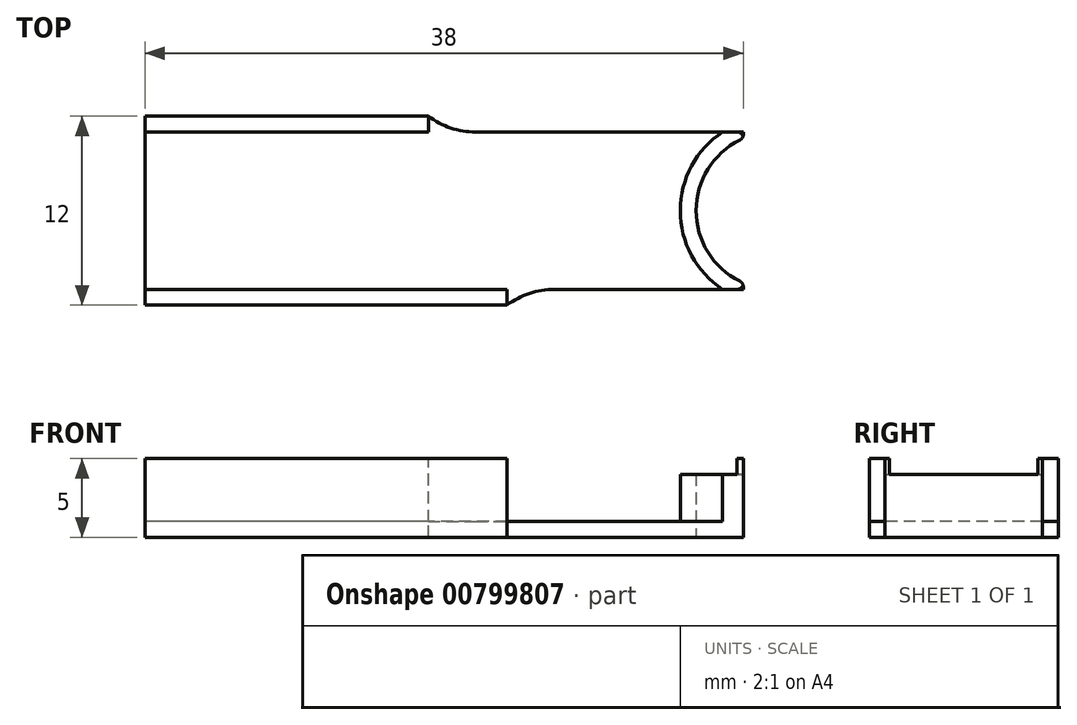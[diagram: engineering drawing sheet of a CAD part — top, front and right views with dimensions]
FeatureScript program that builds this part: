
annotation { "Feature Type Name" : "Feature", "Feature Type Description" : "" }
export const myFeature = defineFeature(function(context is Context, id is Id, definition is map)
    precondition{}
    {
        {
            var Q0;
            Q0=qCreatedBy(makeId("Top.planeOp"),FACE);
            var sketch = newSketch(context, id + "F0", { "sketchPlane" : qUnion([Q0])});
            skLineSegment(sketch, "E0.bottom", {"start": v(0, 0) * mm, "end": v(38, 0) * mm});
            skLineSegment(sketch, "E0.top", {"start": v(0, -12) * mm, "end": v(38, -12) * mm});
            skLineSegment(sketch, "E0.left", {"start": v(0, 0) * mm, "end": v(0, -12) * mm});
            skLineSegment(sketch, "E0.right", {"start": v(38, 0) * mm, "end": v(38, -1.42) * mm});
            skArc(sketch, "E1", {"start": v(38, -1.42) * mm, "mid": v(35, -6) * mm, "end": v(38, -10.58) * mm});
            skPoint(sketch, "E1.centerSnap0", {"position": v(38, -6) * mm});
            skLineSegment(sketch, "E2.trimOffspring", {"start": v(38, -10.58) * mm, "end": v(38, -12) * mm});
            skSolve(sketch);
        }
        {
            var Q0;
            Q0=makeQuery(id+"F0.imprint","IMPRINT",FACE,{"disambiguationData":[TD([[makeQuery(id+"F0.imprint","IMPRINT",EDGE,{"derivedFrom":sQuery(id+"F0.wireOp",EDGE,"E0.bottom")}),-1.0]])]});
            extrude(context, id + "F1", {"entities" : qUnion([Q0]), "depth" : 5 * mm, "offsetDistance" : 25 * mm});
        }
        {
            var Q0;
            Q0=makeQuery(id+"F1.opExtrude","CAP_FACE",FACE,{"disambiguationData":[OSD([sQuery(id+"F0.wireOp",EDGE,"E0.bottom"),sQuery(id+"F0.wireOp",EDGE,"E0.top"),sQuery(id+"F0.wireOp",EDGE,"E0.left"),sQuery(id+"F0.wireOp",EDGE,"E0.right"),sQuery(id+"F0.wireOp",EDGE,"E1"),sQuery(id+"F0.wireOp",EDGE,"E2.trimOffspring")])],"isStart":false});
            var sketch = newSketch(context, id + "F2", { "sketchPlane" : qUnion([Q0])});
            skArc(sketch, "E3.0", {"start": v(38, -1.42) * mm, "mid": v(35, -6) * mm, "end": v(38, -10.58) * mm});
            skArc(sketch, "E4", {"start": v(38, -0.34) * mm, "mid": v(34, -6) * mm, "end": v(38, -11.66) * mm});
            skLineSegment(sketch, "E5", {"start": v(38, -0.34) * mm, "end": v(38, 0) * mm});
            skLineSegment(sketch, "E6", {"start": v(18, -1) * mm, "end": v(0, -1) * mm});
            skLineSegment(sketch, "E7", {"start": v(38, -11.66) * mm, "end": v(38, -12) * mm});
            skLineSegment(sketch, "E8", {"start": v(38, -12) * mm, "end": v(23, -12) * mm});
            skLineSegment(sketch, "E9", {"start": v(23, -12) * mm, "end": v(23, -11) * mm});
            skLineSegment(sketch, "E10", {"start": v(23, -11) * mm, "end": v(0, -11) * mm});
            skLineSegment(sketch, "E11", {"start": v(0, -11) * mm, "end": v(0, -1) * mm});
            skLineSegment(sketch, "E12", {"start": v(18, -1) * mm, "end": v(18, 0) * mm});
            skLineSegment(sketch, "E13", {"start": v(18, 0) * mm, "end": v(38, 0) * mm});
            skSolve(sketch);
        }
        {
            var Q0;
            Q0=makeQuery(id+"F2.imprint","IMPRINT",FACE,{"disambiguationData":[TD([[makeQuery(id+"F2.imprint","IMPRINT",EDGE,{"derivedFrom":sQuery(id+"F2.wireOp",EDGE,"E4")}),-1.0]])]});
            extrude(context, id + "F3", {"entities" : qUnion([Q0]), "operationType" : NewBodyOperationType.REMOVE, "oppositeDirection" : true, "depth" : 4 * mm, "offsetDistance" : 25 * mm});
        }
        {
            var Q0;
            Q0=makeQuery(id+"F1.opExtrude","CAP_FACE",FACE,{"disambiguationData":[OSD([sQuery(id+"F0.wireOp",EDGE,"E0.bottom"),sQuery(id+"F0.wireOp",EDGE,"E0.top"),sQuery(id+"F0.wireOp",EDGE,"E0.left"),sQuery(id+"F0.wireOp",EDGE,"E0.right"),sQuery(id+"F0.wireOp",EDGE,"E1"),sQuery(id+"F0.wireOp",EDGE,"E2.trimOffspring")])],"isStart":true});
            var sketch = newSketch(context, id + "F4", { "sketchPlane" : qUnion([Q0])});
            skLineSegment(sketch, "E14.bottom", {"start": v(38, 12) * mm, "end": v(23, 12) * mm});
            skLineSegment(sketch, "E14.top", {"start": v(38, 11) * mm, "end": v(23, 11) * mm});
            skLineSegment(sketch, "E14.left", {"start": v(38, 12) * mm, "end": v(38, 11) * mm});
            skLineSegment(sketch, "E14.right", {"start": v(23, 12) * mm, "end": v(23, 11) * mm});
            skLineSegment(sketch, "E15.bottom", {"start": v(38, 0) * mm, "end": v(18, 0) * mm});
            skLineSegment(sketch, "E15.top", {"start": v(38, 1) * mm, "end": v(18, 1) * mm});
            skLineSegment(sketch, "E15.left", {"start": v(38, 0) * mm, "end": v(38, 1) * mm});
            skLineSegment(sketch, "E15.right", {"start": v(18, 0) * mm, "end": v(18, 1) * mm});
            skSolve(sketch);
        }
        {
            var Q0;
            Q0=makeQuery(id+"F4.imprint","IMPRINT",FACE,{"disambiguationData":[TD([[makeQuery(id+"F4.imprint","IMPRINT",EDGE,{"derivedFrom":sQuery(id+"F4.wireOp",EDGE,"E14.bottom")}),-1.0]])]});
            var Q1;
            Q1=makeQuery(id+"F4.imprint","IMPRINT",FACE,{"disambiguationData":[TD([[makeQuery(id+"F4.imprint","IMPRINT",EDGE,{"derivedFrom":sQuery(id+"F4.wireOp",EDGE,"E15.bottom")}),1.0]])]});
            extrude(context, id + "F5", {"entities" : qUnion([Q0, Q1]), "operationType" : NewBodyOperationType.REMOVE, "oppositeDirection" : true, "depth" : 25 * mm, "offsetDistance" : 25 * mm});
        }
        {
            var Q0;
            Q0=makeQuery(id+"F1.opExtrude","SWEPT_EDGE",EDGE,{"disambiguationData":[OSD([sQuery(id+"F0.wireOp",EDGE,"E1"),sQuery(id+"F0.wireOp",EDGE,"E2.trimOffspring")])]});
            var Q1;
            Q1=makeQuery(id+"F5.boolean.opBoolean","COPY",EDGE,{"derivedFrom":makeQuery(id+"F5.opExtrude","SWEPT_EDGE",EDGE,{"disambiguationData":[OSD([sQuery(id+"F0.wireOp",EDGE,"E2.trimOffspring"),sQuery(id+"F4.wireOp",EDGE,"E14.top"),sQuery(id+"F4.wireOp",EDGE,"E14.left")])]})});
            var Q2;
            Q2=makeQuery(id+"F1.opExtrude","SWEPT_EDGE",EDGE,{"disambiguationData":[OSD([sQuery(id+"F0.wireOp",EDGE,"E0.right"),sQuery(id+"F0.wireOp",EDGE,"E1")])]});
            var Q3;
            Q3=makeQuery(id+"F5.boolean.opBoolean","COPY",EDGE,{"derivedFrom":makeQuery(id+"F5.opExtrude","SWEPT_EDGE",EDGE,{"disambiguationData":[OSD([sQuery(id+"F0.wireOp",EDGE,"E0.right"),sQuery(id+"F4.wireOp",EDGE,"E15.top"),sQuery(id+"F4.wireOp",EDGE,"E15.left")])]})});
            fillet(context, id + "F6", {"entities" : qUnion([Q0, Q1, Q2, Q3]), "radius" : 0.4 * mm, "tangentPropagation" : true, "allowEdgeOverflow" : false});
        }
        {
            var Q0;
            {var subQ0=sQuery(id+"F0.wireOp",EDGE,"E0.right");var subQ1=sQuery(id+"F0.wireOp",EDGE,"E1");var subQ2=sQuery(id+"F0.wireOp",EDGE,"E2.trimOffspring");Q0=makeQuery(id+"F3.boolean.opBoolean","SPLIT",FACE,{"disambiguationData":[TD([makeQuery(id+"F1.opExtrude","SWEPT_FACE",FACE,{"disambiguationData":[OSD([subQ0])]})])],"derivedFrom":makeQuery(id+"F1.opExtrude","CAP_FACE",FACE,{"disambiguationData":[OSD([sQuery(id+"F0.wireOp",EDGE,"E0.bottom"),sQuery(id+"F0.wireOp",EDGE,"E0.top"),sQuery(id+"F0.wireOp",EDGE,"E0.left"),subQ0,subQ1,subQ2])],"isStart":false})});}
            var sketch = newSketch(context, id + "F7", { "sketchPlane" : qUnion([Q0])});
            skLineSegment(sketch, "E16.0.0", {"start": v(36.68, -11) * mm, "end": v(37.6, -11) * mm});
            skArc(sketch, "E16.0.1", {"start": v(37.6, -11) * mm, "mid": v(37.84, -10.92) * mm, "end": v(37.98, -10.72) * mm});
            skArc(sketch, "E16.0.2", {"start": v(37.98, -10.72) * mm, "mid": v(37.9, -10.58) * mm, "end": v(37.78, -10.48) * mm});
            skArc(sketch, "E16.0.3", {"start": v(37.78, -10.48) * mm, "mid": v(35, -6) * mm, "end": v(37.78, -1.52) * mm});
            skArc(sketch, "E16.0.4", {"start": v(37.78, -1.52) * mm, "mid": v(37.9, -1.42) * mm, "end": v(37.98, -1.28) * mm});
            skArc(sketch, "E16.0.5", {"start": v(37.98, -1.28) * mm, "mid": v(37.84, -1.08) * mm, "end": v(37.6, -1) * mm});
            skLineSegment(sketch, "E16.0.6", {"start": v(37.6, -1) * mm, "end": v(36.68, -1) * mm});
            skArc(sketch, "E16.0.7", {"start": v(36.68, -1) * mm, "mid": v(34, -6) * mm, "end": v(36.68, -11) * mm});
            skSolve(sketch);
        }
        {
            var Q0;
            Q0=makeQuery(id+"F7.imprint","IMPRINT",FACE,{"disambiguationData":[TD([[makeQuery(id+"F7.imprint","IMPRINT",EDGE,{"derivedFrom":sQuery(id+"F7.wireOp",EDGE,"E16.0.0")}),1.0]])]});
            extrude(context, id + "F8", {"entities" : qUnion([Q0]), "operationType" : NewBodyOperationType.REMOVE, "oppositeDirection" : true, "depth" : 1 * mm, "offsetDistance" : 25 * mm});
        }
        {
            var Q0;
            Q0=makeQuery(id+"F5.boolean.opBoolean","COPY",EDGE,{"derivedFrom":makeQuery(id+"F5.opExtrude","SWEPT_EDGE",EDGE,{"disambiguationData":[OSD([sQuery(id+"F4.wireOp",EDGE,"E15.top"),sQuery(id+"F4.wireOp",EDGE,"E15.right")])]})});
            var Q1;
            Q1=makeQuery(id+"F5.boolean.opBoolean","COPY",EDGE,{"derivedFrom":makeQuery(id+"F5.opExtrude","SWEPT_EDGE",EDGE,{"disambiguationData":[OSD([sQuery(id+"F4.wireOp",EDGE,"E14.top"),sQuery(id+"F4.wireOp",EDGE,"E14.right")])]})});
            fillet(context, id + "F9", {"entities" : qUnion([Q0, Q1]), "radius" : 5 * mm, "tangentPropagation" : true, "allowEdgeOverflow" : false});
        }
    });
